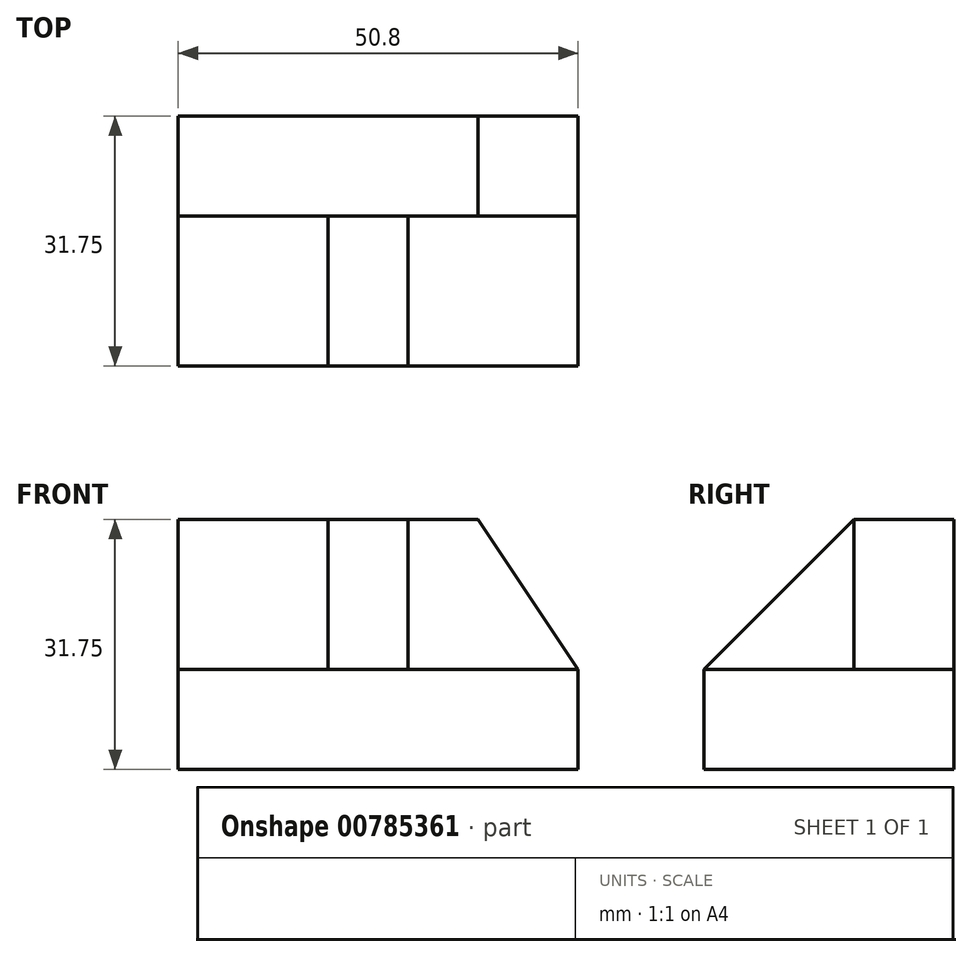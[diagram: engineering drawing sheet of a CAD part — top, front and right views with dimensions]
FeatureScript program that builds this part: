
annotation { "Feature Type Name" : "Feature", "Feature Type Description" : "" }
export const myFeature = defineFeature(function(context is Context, id is Id, definition is map)
    precondition{}
    {
        {
            var Q0;
            Q0=qCreatedBy(makeId("Front.planeOp"),FACE);
            var sketch = newSketch(context, id + "F0", { "sketchPlane" : qUnion([Q0])});
            skLineSegment(sketch, "E0", {"start": v(0, 0) * mm, "end": v(50.8, 0) * mm});
            skLineSegment(sketch, "E1", {"start": v(50.8, 0) * mm, "end": v(50.8, 31.75) * mm});
            skLineSegment(sketch, "E2", {"start": v(50.8, 31.75) * mm, "end": v(0, 31.75) * mm});
            skLineSegment(sketch, "E3", {"start": v(0, 31.75) * mm, "end": v(0, 0) * mm});
            skSolve(sketch);
        }
        {
            var Q0;
            Q0=makeQuery(id+"F0.imprint","IMPRINT",FACE,{"disambiguationData":[TD([[makeQuery(id+"F0.imprint","IMPRINT",EDGE,{"derivedFrom":sQuery(id+"F0.wireOp",EDGE,"E0")}),1.0]])]});
            extrude(context, id + "F1", {"entities" : qUnion([Q0]), "depth" : 31.75 * mm, "offsetDistance" : 25.4 * mm});
        }
        {
            var Q0;
            Q0=makeQuery(id+"F1.opExtrude","SWEPT_FACE",FACE,{"disambiguationData":[OSD([sQuery(id+"F0.wireOp",EDGE,"E3")])]});
            var sketch = newSketch(context, id + "F2", { "sketchPlane" : qUnion([Q0])});
            skLineSegment(sketch, "E4", {"start": v(31.75, 12.7) * mm, "end": v(12.7, 12.7) * mm});
            skLineSegment(sketch, "E5", {"start": v(12.7, 12.7) * mm, "end": v(12.7, 31.75) * mm});
            skLineSegment(sketch, "E6", {"start": v(12.7, 31.75) * mm, "end": v(31.75, 31.75) * mm});
            skLineSegment(sketch, "E7", {"start": v(31.75, 31.75) * mm, "end": v(31.75, 12.7) * mm});
            skSolve(sketch);
        }
        {
            var Q0;
            Q0=makeQuery(id+"F2.imprint","IMPRINT",FACE,{"disambiguationData":[TD([[makeQuery(id+"F2.imprint","IMPRINT",EDGE,{"derivedFrom":sQuery(id+"F2.wireOp",EDGE,"E4")}),-1.0]])]});
            extrude(context, id + "F3", {"entities" : qUnion([Q0]), "operationType" : NewBodyOperationType.REMOVE, "oppositeDirection" : true, "depth" : 19.05 * mm, "offsetDistance" : 25.4 * mm});
        }
        {
            var Q0;
            Q0=makeQuery(id+"F1.opExtrude","SWEPT_FACE",FACE,{"disambiguationData":[OSD([sQuery(id+"F0.wireOp",EDGE,"E1")])]});
            var sketch = newSketch(context, id + "F4", { "sketchPlane" : qUnion([Q0])});
            skLineSegment(sketch, "E8", {"start": v(-31.75, 31.75) * mm, "end": v(-31.75, 12.7) * mm});
            skLineSegment(sketch, "E9", {"start": v(-31.75, 12.7) * mm, "end": v(-12.7, 12.7) * mm});
            skLineSegment(sketch, "E10", {"start": v(-12.7, 12.7) * mm, "end": v(-12.7, 31.75) * mm});
            skLineSegment(sketch, "E11", {"start": v(-12.7, 31.75) * mm, "end": v(-31.75, 31.75) * mm});
            skSolve(sketch);
        }
        {
            var Q0;
            Q0=makeQuery(id+"F4.imprint","IMPRINT",FACE,{"disambiguationData":[TD([[makeQuery(id+"F4.imprint","IMPRINT",EDGE,{"derivedFrom":sQuery(id+"F4.wireOp",EDGE,"E8")}),-1.0]])]});
            extrude(context, id + "F5", {"entities" : qUnion([Q0]), "operationType" : NewBodyOperationType.REMOVE, "oppositeDirection" : true, "depth" : 21.59 * mm, "offsetDistance" : 25.4 * mm});
        }
        {
            var Q0;
            Q0=makeQuery(id+"F5.boolean.opBoolean","COPY",FACE,{"derivedFrom":makeQuery(id+"F5.opExtrude","CAP_FACE",FACE,{"disambiguationData":[OSD([sQuery(id+"F4.wireOp",EDGE,"E8"),sQuery(id+"F4.wireOp",EDGE,"E9"),sQuery(id+"F4.wireOp",EDGE,"E10"),sQuery(id+"F4.wireOp",EDGE,"E11")])],"isStart":false})});
            var sketch = newSketch(context, id + "F6", { "sketchPlane" : qUnion([Q0])});
            skLineSegment(sketch, "E12", {"start": v(-31.75, 12.7) * mm, "end": v(-12.7, 31.75) * mm});
            skLineSegment(sketch, "E13", {"start": v(-31.75, 12.7) * mm, "end": v(-31.75, 31.75) * mm});
            skLineSegment(sketch, "E14", {"start": v(-31.75, 31.75) * mm, "end": v(-12.7, 31.75) * mm});
            skSolve(sketch);
        }
        {
            var Q0;
            Q0=makeQuery(id+"F6.imprint","IMPRINT",FACE,{"disambiguationData":[TD([[makeQuery(id+"F6.imprint","IMPRINT",EDGE,{"derivedFrom":sQuery(id+"F6.wireOp",EDGE,"E12")}),1.0]])]});
            extrude(context, id + "F7", {"entities" : qUnion([Q0]), "operationType" : NewBodyOperationType.REMOVE, "oppositeDirection" : true, "depth" : 25.4 * mm, "offsetDistance" : 25.4 * mm});
        }
        {
            var Q0;
            Q0=makeQuery(id+"F1.opExtrude","CAP_FACE",FACE,{"disambiguationData":[OSD([sQuery(id+"F0.wireOp",EDGE,"E0"),sQuery(id+"F0.wireOp",EDGE,"E1"),sQuery(id+"F0.wireOp",EDGE,"E2"),sQuery(id+"F0.wireOp",EDGE,"E3")])],"isStart":true});
            var sketch = newSketch(context, id + "F8", { "sketchPlane" : qUnion([Q0])});
            skLineSegment(sketch, "E15", {"start": v(-50.8, 31.75) * mm, "end": v(-38.1, 31.75) * mm});
            skLineSegment(sketch, "E16", {"start": v(-50.8, 31.75) * mm, "end": v(-50.8, 12.7) * mm});
            skLineSegment(sketch, "E17", {"start": v(-50.8, 12.7) * mm, "end": v(-38.1, 31.75) * mm});
            skSolve(sketch);
        }
        {
            var Q0;
            Q0=makeQuery(id+"F8.imprint","IMPRINT",FACE,{"disambiguationData":[TD([[makeQuery(id+"F8.imprint","IMPRINT",EDGE,{"derivedFrom":sQuery(id+"F8.wireOp",EDGE,"E15")}),-1.0]])]});
            extrude(context, id + "F9", {"entities" : qUnion([Q0]), "operationType" : NewBodyOperationType.REMOVE, "oppositeDirection" : true, "depth" : 25.4 * mm, "offsetDistance" : 25.4 * mm});
        }
    });
